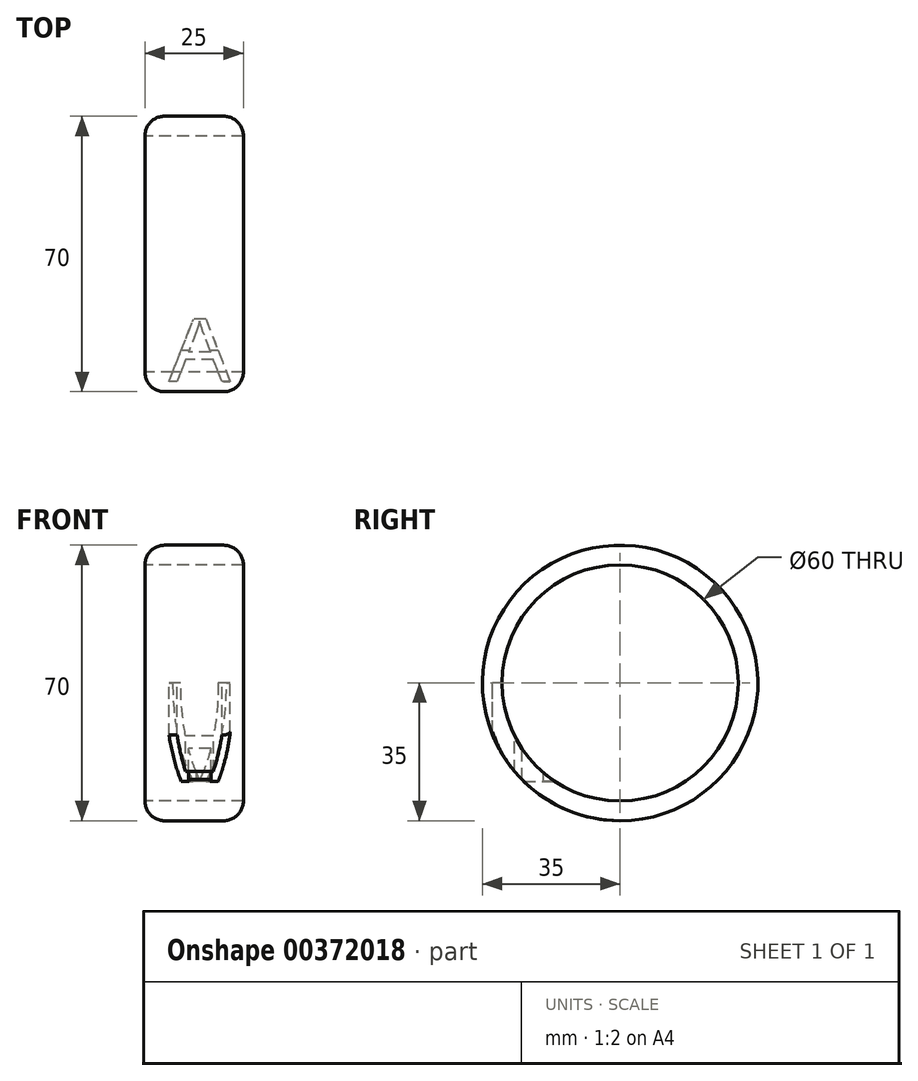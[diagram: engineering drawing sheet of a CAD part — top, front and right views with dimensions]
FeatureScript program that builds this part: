
annotation { "Feature Type Name" : "Feature", "Feature Type Description" : "" }
export const myFeature = defineFeature(function(context is Context, id is Id, definition is map)
    precondition{}
    {
        {
            var Q0;
            Q0=qCreatedBy(makeId("Right.planeOp"),FACE);
            var sketch = newSketch(context, id + "F0", { "sketchPlane" : qUnion([Q0])});
            skCircle(sketch, "E0", {"center": v(0, 0) * mm, "radius": 35 * mm});
            skCircle(sketch, "E1", {"center": v(0, 0) * mm, "radius": 30 * mm});
            skSolve(sketch);
        }
        {
            var Q0;
            Q0=makeQuery(id+"F0.imprint","IMPRINT",FACE,{"disambiguationData":[TD([[makeQuery(id+"F0.imprint","IMPRINT",EDGE,{"derivedFrom":sQuery(id+"F0.wireOp",EDGE,"E0")}),1.0]])]});
            extrude(context, id + "F1", {"entities" : qUnion([Q0]), "offsetDistance" : 25 * mm, "depth" : 25 * mm});
        }
        {
            var Q0;
            Q0=makeQuery(id+"F1.opExtrude","SWEPT_FACE",FACE,{"disambiguationData":[OSD([sQuery(id+"F0.wireOp",EDGE,"E0")])]});
            fillet(context, id + "F2", {"entities" : qUnion([Q0]), "radius" : 5 * mm, "tangentPropagation" : true, "allowEdgeOverflow" : false});
        }
        {
            var Q0;
            Q0=qCreatedBy(makeId("Top.planeOp"),FACE);
            var sketch = newSketch(context, id + "F3", { "sketchPlane" : qUnion([Q0])});
            skText(sketch, "E2", { "text": "A", "fontName": "OpenSans-Regular.ttf"});
            const initialGuessF3  = {"E2": [0.0061, -0.0324, 1, 0, 0.01772]};
            skSetInitialGuess(sketch, initialGuessF3);
            skSolve(sketch);
        }
        {
            var Q0;
            Q0 = qSketchRegion(id + "F3", true);
            extrude(context, id + "F4", {"entities" : qUnion([Q0]), "operationType" : NewBodyOperationType.REMOVE, "oppositeDirection" : true, "depth" : 25 * mm, "offsetDistance" : 25 * mm});
        }
    });
